# Revit family: Plumbing_Other-Plumbing_Menzies-Metal_Plumbing-Stack-Spun-Aluminum-Flat-Welded-TPO (1)
name_source: partatom
category: Plumbing Fixtures
revit_build: Autodesk Revit 2018 (Build: 20170223_1515(x64)
units: mm (PartAtom-declared; Revit-internal decimal feet)

## family parameters
Cut with Voids When Loaded = No
Host = Face
OmniClass Number = 23.70.50.21.24.11
OmniClass Title = Roof Waste Water Drains
Part Type = Normal
Room Calculation Point = No
Round Connector Dimension = Use Diameter
Shared = No

## types (1)
- Refer to Type Catalog
    Assembly Code = D2040200
    CW Connection = No
    Default Elevation = 48 "
    Description = Plumbing Stack Spun Aluminum - Flat Welded-TPO
    Drain Flow = 0 GPM
    Edition number = 1
    HW Connection = No
    Manufacturer = Menzies Metal Products
    Model = 400-3110TPO
    Pipe Diameter = 2"
    Pipe Length = 12 "
    Product Guid = 03c8de97-1602-48cd-85a9-ab49e266789e
    Product Material = Metal - Menzies Metal Products - Aluminium TPO Coated
    Product data url = https://www.bimobject.com
    URL = https://www.menzies-metal.com
    Vent Connection = No
    Waste Connection = No
    Weight = 1.00 lbf

## geometry (parser evidence)
native form markers: Sweep x5
no freeform markers — native parametric forms only
